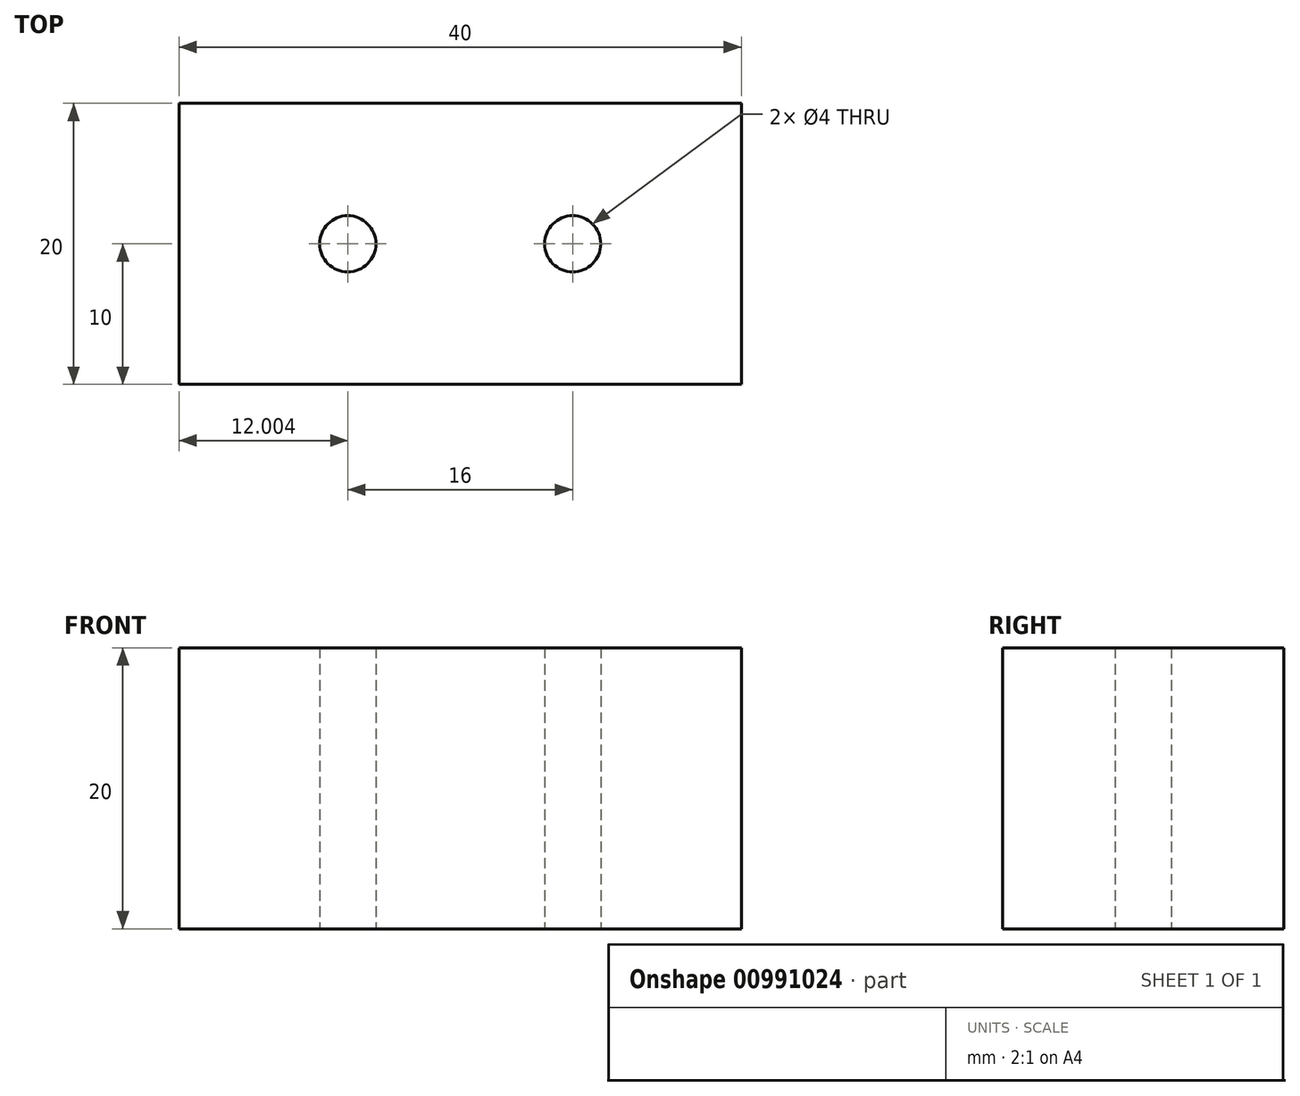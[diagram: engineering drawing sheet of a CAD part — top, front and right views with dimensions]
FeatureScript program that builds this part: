
annotation { "Feature Type Name" : "Feature", "Feature Type Description" : "" }
export const myFeature = defineFeature(function(context is Context, id is Id, definition is map)
    precondition{}
    {
        {
            var Q0;
            Q0=qCreatedBy(makeId("Top.planeOp"),FACE);
            var sketch = newSketch(context, id + "F0", { "sketchPlane" : qUnion([Q0])});
            skLineSegment(sketch, "E0.top", {"start": v(-32.64, -10) * mm, "end": v(7.36, -10) * mm});
            skLineSegment(sketch, "E0.left", {"start": v(-32.64, 10) * mm, "end": v(-32.64, -10) * mm});
            skLineSegment(sketch, "E0.right", {"start": v(7.36, 10) * mm, "end": v(7.36, -10) * mm});
            skLineSegment(sketch, "E1.bottom", {"start": v(0, 0) * mm, "end": v(0, 0) * mm});
            skLineSegment(sketch, "E2", {"start": v(-32.64, 10) * mm, "end": v(7.36, 10) * mm});
            skCircle(sketch, "E3", {"center": v(-20.64, 0) * mm, "radius": 2 * mm});
            skCircle(sketch, "E4", {"center": v(-4.64, 0) * mm, "radius": 2 * mm});
            skSolve(sketch);
        }
        {
            var Q0;
            Q0 = qSketchRegion(id + "F0", true);
            extrude(context, id + "F1", {"entities" : qUnion([Q0]), "depth" : 20 * mm, "offsetDistance" : 25 * mm});
        }
    });
